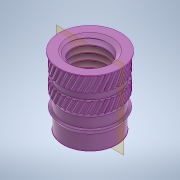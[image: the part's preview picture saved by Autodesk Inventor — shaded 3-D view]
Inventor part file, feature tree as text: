
AUTODESK INVENTOR PART (.ipt)
format: ipt  version: 2021.1 (Build 251245000, 245)  size: 977,408 bytes
history: native  units: in
note: dims shown in document units (in); Inventor stores cm internally (conversion verified against a paired STEP export)
features: revolve x1, sketch x1, other x1
ambient origin geometry x8: Origin, YZ Plane, XZ Plane, XY Plane, X Axis, Y Axis, Z Axis, Center Point
bodies: Solid1 (feature_tree)
feature tree (3):
  revolve  "Revolution1"  [1 undecoded]
  sketch  "Sketch2"  dims[d2=0.2422in d3=0.055in d4=0.1543in d5=90.0deg]
  other  "Cut-Revolve1"
note: 1 required parameter value undecoded (feature->parameter linkage not recoverable at this tier; creation-order binding heuristic only, values carry confidence <= 0.55)
